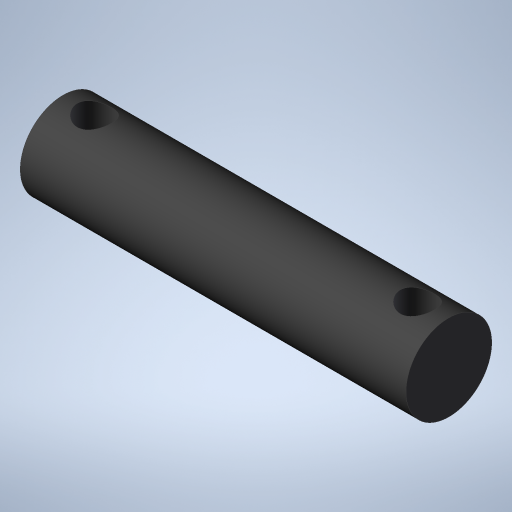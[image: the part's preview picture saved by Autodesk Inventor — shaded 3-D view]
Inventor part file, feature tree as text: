
AUTODESK INVENTOR PART (.ipt)
format: ipt  version: 2023 (Build 270158000, 158)  size: 244,224 bytes
history: native  units: in
note: dims shown in document units (in); Inventor stores cm internally (conversion verified against a paired STEP export)
features: extrude x2, sketch x2, plane x1
ambient origin geometry x8: Origin, YZ Plane, XZ Plane, XY Plane, X Axis, Y Axis, Z Axis, Center Point
bodies: Solid1 (feature_tree)
feature tree (5):
  extrude  "Extrusion1"  Depth=1.125in TaperAngle=0.0deg
  plane  "Work Plane1"
  extrude  "Extrusion2"  Depth=0.471in
  sketch  "Sketch1"  dims[d0=0.25in d1=1.125in d2=0.0in]
  sketch  "Sketch2"  dims[d3=0.1875in d4=0.471in d5=0.471in d6=0.1in d7=1.0in d8=0.0in d9=0.1in]
